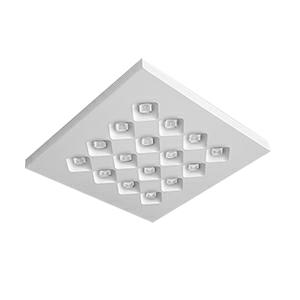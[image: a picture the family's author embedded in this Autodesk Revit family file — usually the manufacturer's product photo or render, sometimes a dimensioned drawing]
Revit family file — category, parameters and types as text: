
# Revit family: 3f_filippi_-_3f_diagon_soft_ugr_3f_filippi_-_23828_a0686_-_3f_diagon_25w-830_dali_soft_ugr_596x596___corn_plaf__cae3
name_source: partatom
category: Lighting Fixtures
units: mm (PartAtom-declared; Revit-internal decimal feet)

## family parameters
Cut with Voids When Loaded = No
Host = Face
Light Source = No
Part Type = Normal
Room Calculation Point = No
Round Connector Dimension = Use Diameter
Shared = No

## types (1)
- 3F Filippi - 3F Dìagon Soft UGR (1 x LED, 3495 lm, 28 W, 3000 K)
    Apparent Load = 28 VA
    Approval mark = CE
    CIE Flux Codes = 59 92 100 100 100
    Color Rendering = 80
    Color Temperature = 3000 K
    Control Gear = Electronic transformer
    Default Elevation = 1800 mm
    Description = ILLUMINOTECHNICAL
Luminous efficiency 100% (DLOR 100%, ULOR 0%).
Initial luminous flux of the luminaire 3495 lm.
Direct symmetric distribution.
Installation Interdistance Transv.D = 1.23 x hu - Long.D = 1.23 x hu.
Average luminance <3000 cd/m² for radial angles >65°.
Tabular UGR (CIE 117 - 4H-8H; S=0.25H; 70/50/20): RUG 18.6 - 18.5.
Beam angle: 102° - 101°.
Luminous efficacy 125 lm/W.
Lifetime (L95/B10): 30000 h. (tq+25°C)
Lifetime (L90/B10): 50000 h. (tq+25°C)
Lifetime (L80/B10): 80000 h. (tq+25°C)
Lifetime (L75/B10): 100000 h. (tq+25°C)
Sudden decreased luminous flux after 50000 hours: 0% (C0).
Photobiological safety in compliance with IEC/TR 62778: RG0 risk exempt, (IEC 62471).
In compliance with IEC/EN 62722-2-1 - IEC/EN 62717 standards.

SOURCE
Squared LED module 25W/830.
Energy efficiency class (UE 2019/2020 - UE 2019/2015): C.
CIE 13.3 Colour rendering index: CRI >80 (R9 <50%).
IES TM-30 Fidelity Index: Rf = 84 Rg = 95.
CCT nominal colour temperature 3000 K.
Colour initial tolerance (MacAdam): SDCM 3.

MECHANICAL
Housing in hot-galvanised steel, painted in white polyester.
Honeycombed diagonal screen in white anti-glare polycarbonate.
Opal methacrylate (PMMA) rhomboid lenses with differentiated, engraved and prismatic surfaces for diffused, soft lighting and excellent visual comfort.
Luminaire with limited surface temperature. - D - (EN 60598-2-24)
Dimensions: 600x600 mm, height 40 mm. Weight 6.225 kg.
IP43 protection degree for exposed part, IP20 for recessed part.
Mechanical strength to impacts IK06 (1 joule).
Glow-wire test resistance 650°C.

ELECTRICAL
Halogen Free DALI-2, PUSH-DIM, electronic wiring 230V-50/60Hz, power factor 0.95 at full load, THD <25%, constant output current, class I, 1 driver, 1 DALI addresse.
Power of the luminaire 28 W.
ENEC - CE.
SAFE FLICKER: PstLM=<1 and SVM=<0.4 (IEC TR 61547-1 and IEC TR 63158), to ensure a more comfortable and safe light.
Luminaire compliant with EN 60598-2-22 for power supply from a centralised emergency system CPSS (Central Power Supply System), not incorporated in the luminaire - high risk areas excluded. The default power and flux are 100% in AC and 15% in DC.
Ambient temperature from 0°C to +25°C.
Temperature class T6 max 85°C.
Quick connection.
Relative humidity UR: <85%.

INSTALLATION
Ceiling.
Height only 40 mm.
All accessories dedicated to this product are available on the Catalog and on our website www.3F-Filippi.com.

ACCESSORIES
A0686 - 596x596 Diagon frame for Ceiling installation.

APPLICATIONS
Environments: staterooms, with VDTs, offices.
Environments with exacting visual tasks, where diffused soft light for optimum visual comfort is required.

LIGHT MANAGEMENT
Recommended minimum setting: 10%.
The device, equipped with DALI-2 driver, can be controlled manually with 3F Easy Dim technology or automatically/manually with 3F Smart Dimming technology and/or centralised DALI systems.
DALI-2 certification guarantees interoperability with other devices with the same certification.
In electrical systems without a regulation system (manual or automatic) and DALI bus, a suitable jumper must be made on the DA-DA terminals of the appliance.

WARNING
Luminaire designed for disposal/recycling at end-of-life.
Replaceable (LED only) light source by a professional. Replaceable control gear by a professional.
    Height = 0 mm  [stored 0 ft]
    Lamp = 1 x LED
    Lamp Light Flux = 3495 lm
    Lamp Power = 28 W
    Lamp count = 1
    Length = 600 mm
    Lifetime = 50000 h
    Luminous efficacy = 125 lm/W
    Manufacturer = 3F Filippi
    ModVariant = No
    Model = 3F Filippi - 23828+A0686 - 3F Diagon 25W-830 DALI SOFT UGR 596x596 + Corn.plaf.
    Mounting Place = Ceiling
    Mounting Type = Recessed
    Number of Poles = 1
    OnlyDefault = Yes
    Power Factor = 1
    Product Name = 3F Filippi - 3F Dìagon Soft UGR
    Product group = recessed luminaire
    ProductGroupID = 4
    Protection Class = Protection class I
    Protection Degree = IP 20
    RLX_Detail_Level = 1
    RLX_Emergency_Light_Flux = 0 lm
    RLX_Emergency_Type = 0
    RLX_Emergency_Type_DB = No
    RlxData = <blob elided: 97753 chars, md5=c2086167>
    Socket = socket
    Standby Power = 0 W
    System Light Flux = 3495 lm
    System Power = 28 W
    Type Comments = Product without accessories
    Type Image = 3ffilippi_3f_diagon__a0686.jpg
    URL = http://relux.com
    VarID = ---
    Voltage = 0 V
    Weight = 0.00 kg
    Width = 600 mm

note: [stored X ft] marks values corroborated as IEEE doubles in the binary element streams (Revit-internal decimal feet)

## geometry (parser evidence)
native form markers: Blend x4, Sweep x9
no freeform markers — native parametric forms only
